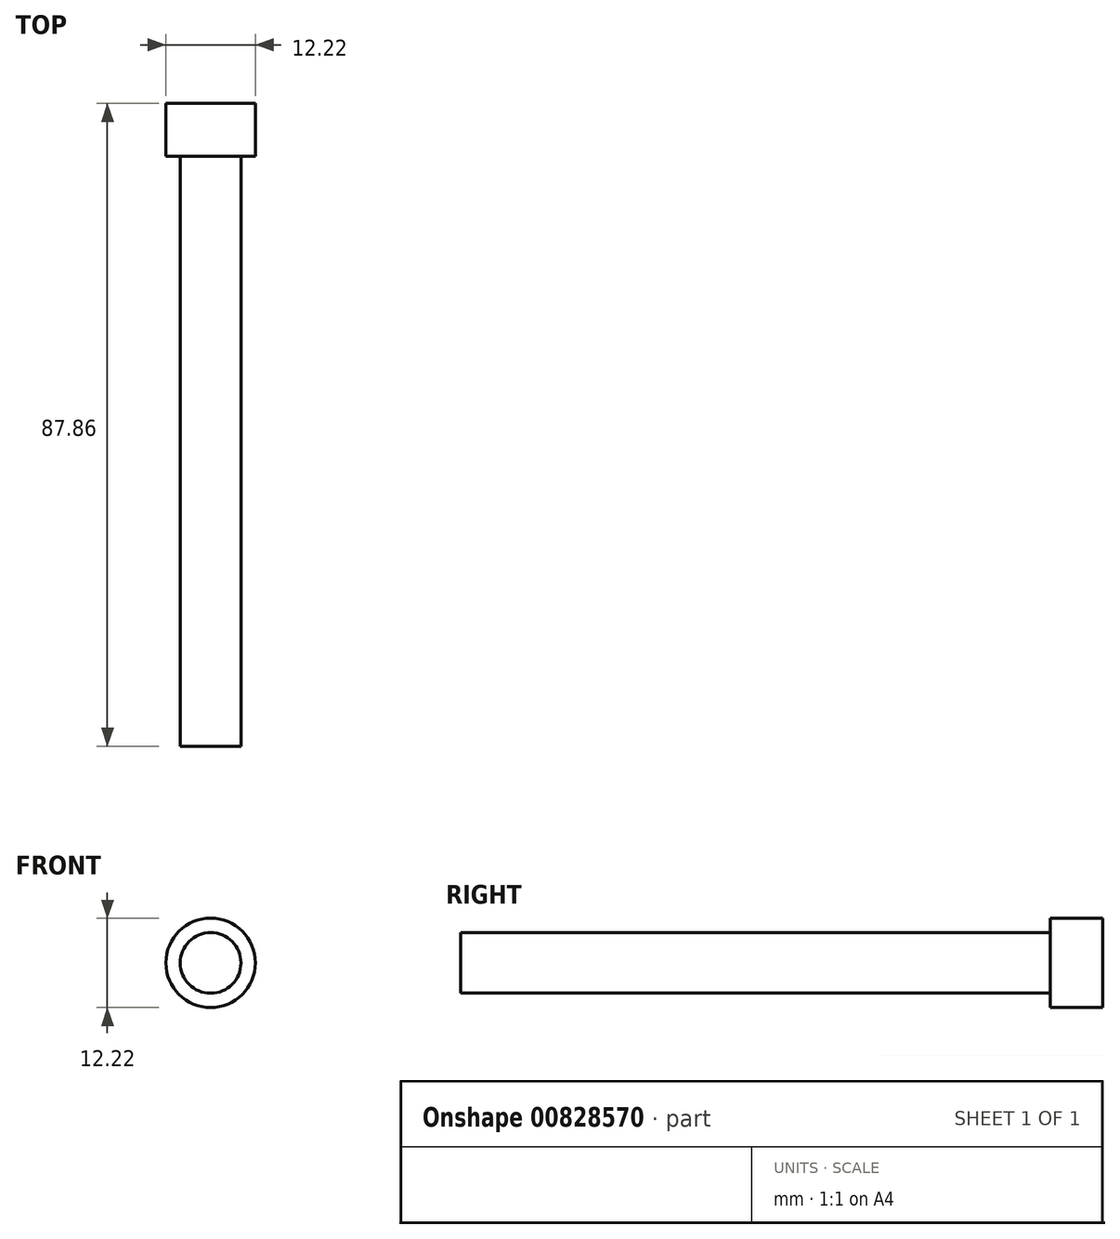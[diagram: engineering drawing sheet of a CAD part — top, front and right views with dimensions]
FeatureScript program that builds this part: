
annotation { "Feature Type Name" : "Feature", "Feature Type Description" : "" }
export const myFeature = defineFeature(function(context is Context, id is Id, definition is map)
    precondition{}
    {
        {
            var Q0;
            Q0=qCreatedBy(makeId("Top.planeOp"),FACE);
            var sketch = newSketch(context, id + "F0", { "sketchPlane" : qUnion([Q0])});
            skLineSegment(sketch, "E0", {"start": v(-25.27, 0) * mm, "end": v(-25.27, -60.19) * mm});
            skLineSegment(sketch, "E1", {"start": v(-25.27, 0) * mm, "end": v(-25.27, 20.47) * mm});
            skLineSegment(sketch, "E2", {"start": v(-25.27, 20.47) * mm, "end": v(-27.23, 20.47) * mm});
            skLineSegment(sketch, "E3", {"start": v(-27.23, 20.47) * mm, "end": v(-27.23, 27.67) * mm});
            skLineSegment(sketch, "E4", {"start": v(-21.12, 27.67) * mm, "end": v(-21.12, -60.19) * mm});
            skPoint(sketch, "E4.startSnap0", {"position": v(-21.12, 20.47) * mm});
            skLineSegment(sketch, "E5", {"start": v(-21.12, -60.19) * mm, "end": v(-25.27, -60.19) * mm});
            skLineSegment(sketch, "E6", {"start": v(-27.23, 27.67) * mm, "end": v(-21.12, 27.67) * mm});
            skSolve(sketch);
        }
        {
            var Q0;
            Q0=makeQuery(id+"F0.imprint","IMPRINT",FACE,{"disambiguationData":[TD([[makeQuery(id+"F0.imprint","IMPRINT",EDGE,{"derivedFrom":sQuery(id+"F0.wireOp",EDGE,"E0")}),1.0]])]});
            var Q1;
            Q1=sQuery(id+"F0.wireOp",EDGE,"E4");
            revolve(context, id + "F1", {"surfaceOperationType" : NewSurfaceOperationType.NEW, "entities" : qUnion([Q0]), "axis" : qUnion([Q1]), "revolveType" : RevolveType.FULL});
        }
    });
